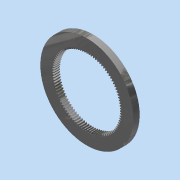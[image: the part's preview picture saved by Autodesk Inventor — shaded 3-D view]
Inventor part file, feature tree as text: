
AUTODESK INVENTOR PART (.ipt)
format: ipt  version: 2015 (Build 190159000, 159)  size: 460,800 bytes
history: native  units: in
note: dims shown in document units (in); Inventor stores cm internally (conversion verified against a paired STEP export)
features: other x1, direct_edit x1, pattern_circular x1, imported_body x1, move_body x1
ambient origin geometry x8: Origin, YZ Plane, XZ Plane, XY Plane, X Axis, Y Axis, Z Axis, Center Point
bodies: Solid1 (feature_tree)
feature tree (5):
  other  "a_1b10-n480961"
  direct_edit  "Direct Edit1"
  pattern_circular  "Circular Pattern1"  [2 undecoded]
  imported_body  "Base1"
  move_body  "Move1"
note: 2 required parameter values undecoded (feature->parameter linkage not recoverable at this tier; creation-order binding heuristic only, values carry confidence <= 0.55)
